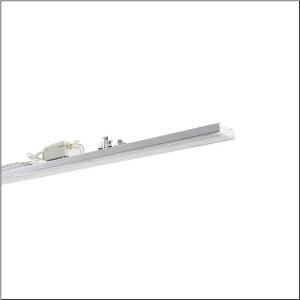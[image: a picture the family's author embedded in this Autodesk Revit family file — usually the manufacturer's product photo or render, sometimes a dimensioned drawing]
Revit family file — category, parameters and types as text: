
# Revit family: licross_21_recessed_mo_52te19dv4e5g
name_source: partatom
category: Lighting Fixtures
units: mm (PartAtom-declared; Revit-internal decimal feet)

## family parameters
Cut with Voids When Loaded = No
Host = Face
Light Source = No
Part Type = Normal
Room Calculation Point = No
Round Connector Dimension = Use Diameter
Shared = No

## types (1)
- --- (1 x LED, 14780 lm, 85.3 W, 4000K)
    Apparent Load = 85 VA
    CIE Flux Codes = 55 90 98 100 100
    Color Rendering = 80
    Color Temperature = 4000K
    Default Elevation = 1800 mm
    Description = Licross 21 Recessed MO, luminaire insert, of sheet steel, galvanised, coil coated, white, length: 2.250mm, width: 66mm, height: 67mm, LED rated luminous flux: 14.780lm, light colour: 840, SDCM (Standard Deviation of Colour Matching)MacAdam ≤ 3 SDCM (initial), control gear: DALI 2, with plug, 5-pole, with phase selection, mains connection: 220..240V, AC, 50/60Hz, rated input power: 85W, internal wiring halogen-free, primary light control with lens, of plastic, primary optical cover: cover, of PMMA, light emission: direct distribution, primary light characteristic: double asymmetric, protection rating (complete): IP54, insulation class (complete): insulation class I (protective earthing), certification: CE, ENEC, VDE, UKCA, protection symbol: D if used in an environment with non-conductive dust loads with corresponding accessories, impact resistance: IK06, permissible ambient temperature for indoor applications: -25..+35°C, corresponds to IFS (International Featured Standards) requirements for safety and quality in the food industry, reducing of maximum allowable ambient temperature of 5°C with ceiling mounting, LABS conformity tested according to VDMA 24364:2018-05, The light source and the operating device comply with the requirements of the Ecodesign Regulation (EU) 2019/2020 and are replaceable in accordance with this regulation, packaging unit: 1 piece
    Height = 58 mm
    Lamp = 1 x LED
    Lamp Light Flux = 14780 lm
    Lamp Power = 85.3 W
    Lamp count = 1
    Length = 2250 mm
    Luminous efficacy = 173 lm/W
    Manufacturer = Siteco
    ModVariant = No
    Model = 52TE19DV4E5G
    Mounting Place = Ceiling
    Mounting Type = Pendant
    Number of Poles = 1
    OnlyDefault = Yes
    Power Factor = 1
    Product Name = Licross 21 Recessed MO
    Product group = luminaire insert | ceiling pendant
    ProductGroupID = 901
    Protection Class = Protection class I
    Protection Degree = IP 54
    RLX_Detail_Level = 1
    RLX_Emergency_Light_Flux = 0 lm
    RLX_Emergency_Type = 0
    RLX_Emergency_Type_DB = No
    RlxData = <blob elided: 29813 chars, md5=e336d97a>
    Socket = socket
    Standby Power = 0 W
    System Light Flux = 14780 lm
    System Power = 85 W
    Type Comments = factory setting: luminous flux: 100 % | dim-lin: 254 | 390 mA
    Type Image = l_1296930.jpg
    URL = http://relux.com
    VarID = @adj_129731
    Voltage = 0 V
    Weight = 0.00 kg
    Width = 66 mm

## geometry (parser evidence)
native form markers: Blend x4, Sweep x11
no freeform markers — native parametric forms only
